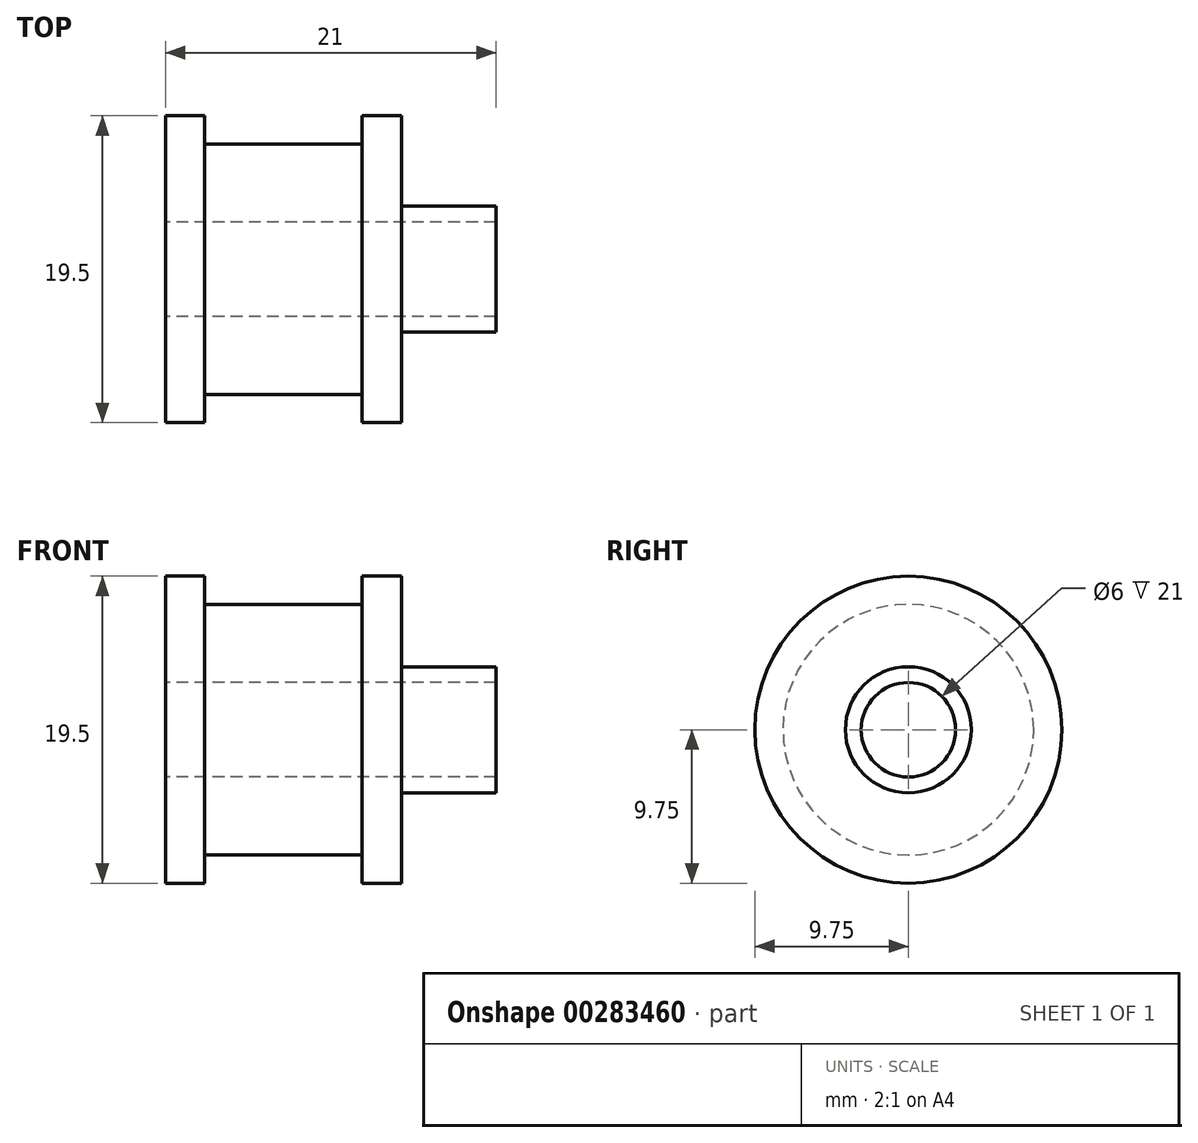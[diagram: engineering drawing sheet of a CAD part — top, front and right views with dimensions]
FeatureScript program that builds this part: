
annotation { "Feature Type Name" : "Feature", "Feature Type Description" : "" }
export const myFeature = defineFeature(function(context is Context, id is Id, definition is map)
    precondition{}
    {
        {
            var Q0;
            Q0=qCreatedBy(makeId("Front.planeOp"),FACE);
            var sketch = newSketch(context, id + "F0", { "sketchPlane" : qUnion([Q0])});
            skLineSegment(sketch, "E0", {"start": v(-18.22, 0) * mm, "end": v(20.5, 0) * mm, "construction": true});
            skLineSegment(sketch, "E1", {"start": v(6, 3) * mm, "end": v(-15, 3) * mm});
            skLineSegment(sketch, "E2", {"start": v(-15, 3) * mm, "end": v(-15, 9.75) * mm});
            skLineSegment(sketch, "E3", {"start": v(-15, 9.75) * mm, "end": v(-12.5, 9.75) * mm});
            skLineSegment(sketch, "E4", {"start": v(-12.5, 9.75) * mm, "end": v(-12.5, 7.96) * mm});
            skLineSegment(sketch, "E5", {"start": v(-12.5, 7.96) * mm, "end": v(-2.5, 7.96) * mm});
            skLineSegment(sketch, "E6", {"start": v(-2.5, 7.96) * mm, "end": v(-2.5, 9.75) * mm});
            skLineSegment(sketch, "E7", {"start": v(-2.5, 9.75) * mm, "end": v(0, 9.75) * mm});
            skLineSegment(sketch, "E8", {"start": v(0, 9.75) * mm, "end": v(0, 4) * mm});
            skLineSegment(sketch, "E9", {"start": v(0, 4) * mm, "end": v(6, 4) * mm});
            skLineSegment(sketch, "E10", {"start": v(6, 4) * mm, "end": v(6, 3) * mm});
            skSolve(sketch);
        }
        {
            var Q0;
            Q0 = qSketchRegion(id + "F0", true);
            var Q1;
            Q1=sQuery(id+"F0.wireOp",EDGE,"E0");
            revolve(context, id + "F1", {"entities" : qUnion([Q0]), "axis" : qUnion([Q1]), "revolveType" : RevolveType.FULL});
        }
    });
